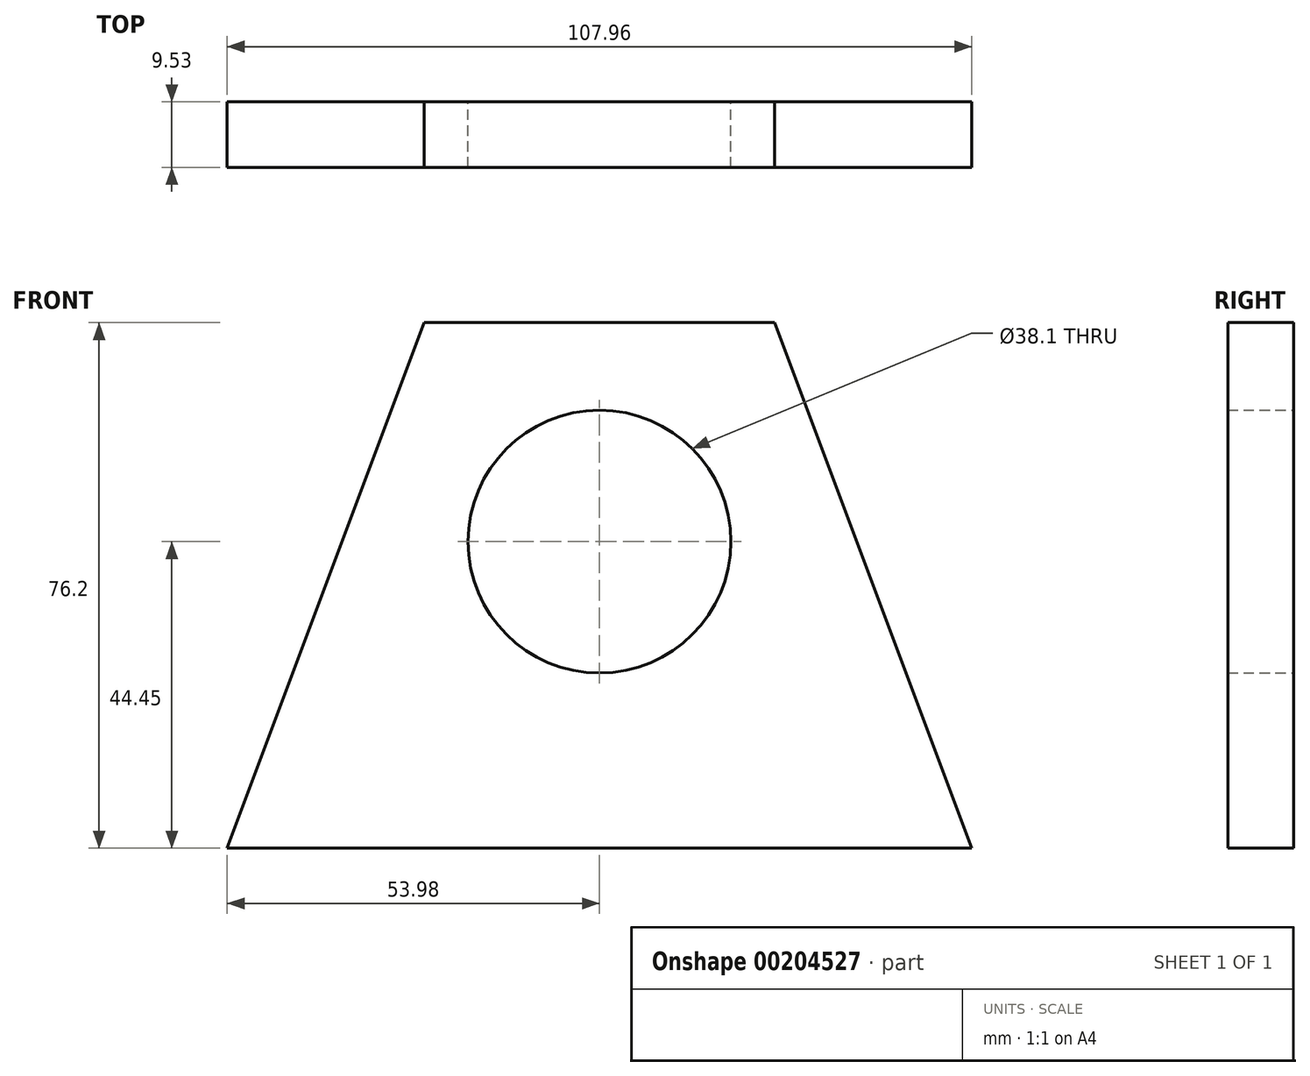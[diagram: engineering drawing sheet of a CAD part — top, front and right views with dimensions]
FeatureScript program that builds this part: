
annotation { "Feature Type Name" : "Feature", "Feature Type Description" : "" }
export const myFeature = defineFeature(function(context is Context, id is Id, definition is map)
    precondition{}
    {
        {
            var Q0;
            Q0=qCreatedBy(makeId("Front.planeOp"),FACE);
            var sketch = newSketch(context, id + "F0", { "sketchPlane" : qUnion([Q0])});
            skLineSegment(sketch, "E0", {"start": v(-53.97, 0) * mm, "end": v(53.97, 0) * mm});
            skLineSegment(sketch, "E1", {"start": v(-53.97, 0) * mm, "end": v(-25.4, 76.2) * mm});
            skLineSegment(sketch, "E2.MirrorCS", {"start": v(53.98, 0) * mm, "end": v(25.4, 76.2) * mm});
            skLineSegment(sketch, "E3", {"start": v(-25.4, 76.2) * mm, "end": v(25.4, 76.2) * mm});
            skCircle(sketch, "E4", {"center": v(0, 44.45) * mm, "radius": 19.05 * mm});
            skSolve(sketch);
        }
        {
            var Q0;
            Q0=makeQuery(id+"F0.imprint","IMPRINT",FACE,{"disambiguationData":[TD([[makeQuery(id+"F0.imprint","IMPRINT",EDGE,{"derivedFrom":sQuery(id+"F0.wireOp",EDGE,"E0")}),1.0]])]});
            extrude(context, id + "F1", {"entities" : qUnion([Q0]), "depth" : 9.52 * mm});
        }
    });
